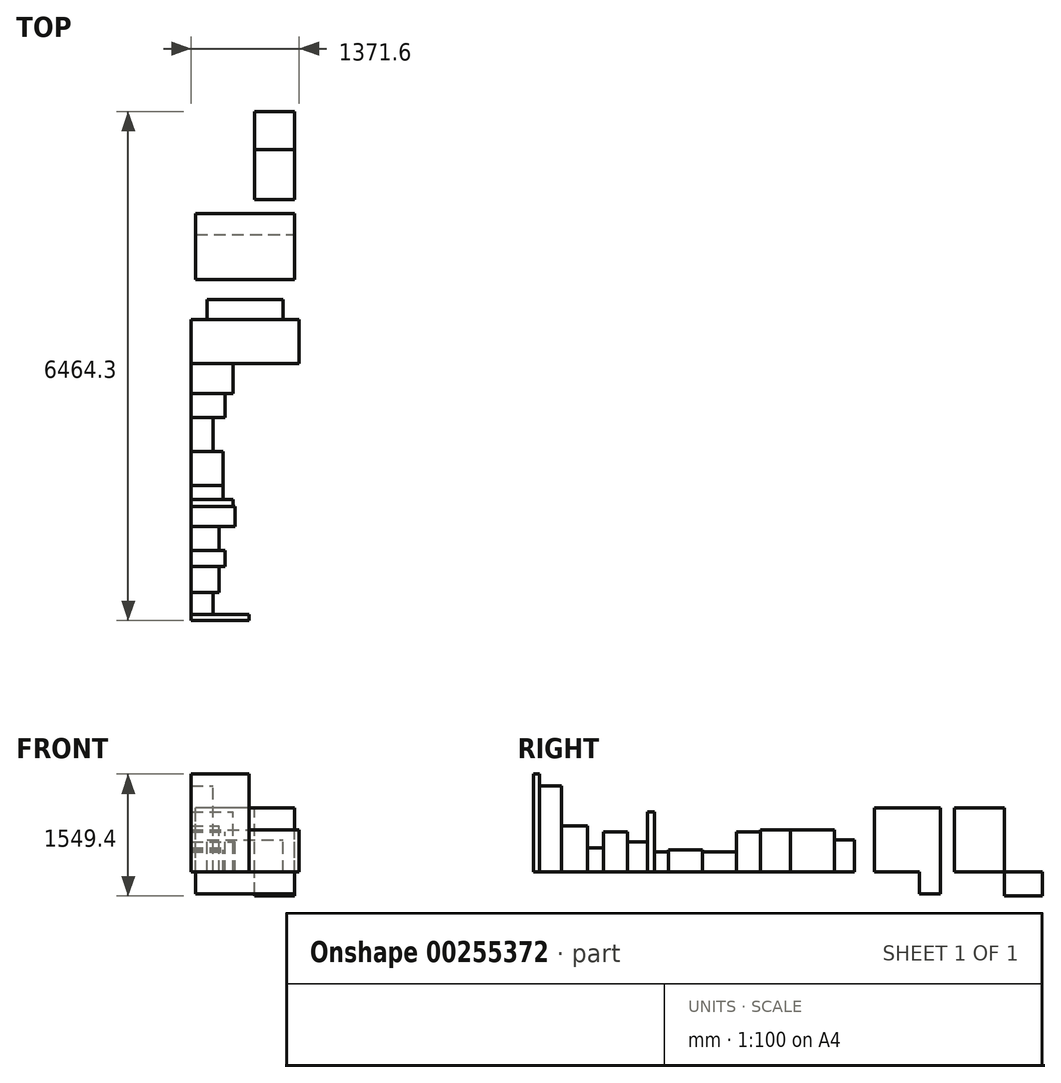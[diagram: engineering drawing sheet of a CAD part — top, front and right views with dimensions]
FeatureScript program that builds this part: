
annotation { "Feature Type Name" : "Feature", "Feature Type Description" : "" }
export const myFeature = defineFeature(function(context is Context, id is Id, definition is map)
    precondition{}
    {
        {
            var Q0;
            Q0=qCreatedBy(makeId("Front.planeOp"),FACE);
            var sketch = newSketch(context, id + "F0", { "sketchPlane" : qUnion([Q0])});
            skLineSegment(sketch, "E0.bottom", {"start": v(0, 0) * mm, "end": v(965.2, 0) * mm});
            skLineSegment(sketch, "E0.top", {"start": v(0, 406.4) * mm, "end": v(965.2, 406.4) * mm});
            skLineSegment(sketch, "E0.left", {"start": v(0, 0) * mm, "end": v(0, 406.4) * mm});
            skLineSegment(sketch, "E0.right", {"start": v(965.2, 0) * mm, "end": v(965.2, 406.4) * mm});
            skSolve(sketch);
        }
        {
            var Q0;
            Q0 = qSketchRegion(id + "F0", true);
            extrude(context, id + "F1", {"entities" : qUnion([Q0]), "depth" : 254 * mm});
        }
        {
            var Q0;
            Q0=makeQuery(id+"F1.opExtrude","CAP_FACE",FACE,{"disambiguationData":[OSD([sQuery(id+"F0.wireOp",EDGE,"E0.bottom"),sQuery(id+"F0.wireOp",EDGE,"E0.top"),sQuery(id+"F0.wireOp",EDGE,"E0.left"),sQuery(id+"F0.wireOp",EDGE,"E0.right")])],"isStart":false});
            var sketch = newSketch(context, id + "F2", { "sketchPlane" : qUnion([Q0])});
            skLineSegment(sketch, "E1.bottom", {"start": v(-203.2, 533.4) * mm, "end": v(1168.4, 533.4) * mm});
            skLineSegment(sketch, "E1.top", {"start": v(-203.2, 0) * mm, "end": v(1168.4, 0) * mm});
            skLineSegment(sketch, "E1.left", {"start": v(-203.2, 533.4) * mm, "end": v(-203.2, 0) * mm});
            skLineSegment(sketch, "E1.right", {"start": v(1168.4, 533.4) * mm, "end": v(1168.4, 0) * mm});
            skSolve(sketch);
        }
        {
            var Q0;
            Q0 = qSketchRegion(id + "F2", true);
            extrude(context, id + "F3", {"entities" : qUnion([Q0]), "operationType" : NewBodyOperationType.ADD, "depth" : 558.8 * mm});
        }
        {
            var Q0;
            Q0=makeQuery(id+"F1.opExtrude","CAP_FACE",FACE,{"disambiguationData":[OSD([sQuery(id+"F0.wireOp",EDGE,"E0.bottom"),sQuery(id+"F0.wireOp",EDGE,"E0.top"),sQuery(id+"F0.wireOp",EDGE,"E0.left"),sQuery(id+"F0.wireOp",EDGE,"E0.right")])],"isStart":true});
            cPlane(context, id + "F4", {"entities" : qUnion([Q0]), "cplaneType" : CPlaneType.OFFSET, "offset" : 254 * mm, "width" : 152.4 * mm, "height" : 152.4 * mm});
        }
        {
            var Q0;
            Q0=qCreatedBy(id+"F4.planeOp",FACE);
            var sketch = newSketch(context, id + "F5", { "sketchPlane" : qUnion([Q0])});
            skLineSegment(sketch, "E2.bottom", {"start": v(-1111.25, 0) * mm, "end": v(146.05, 0) * mm});
            skLineSegment(sketch, "E2.top", {"start": v(-1111.25, 812.8) * mm, "end": v(146.05, 812.8) * mm});
            skLineSegment(sketch, "E2.left", {"start": v(-1111.25, 0) * mm, "end": v(-1111.25, 812.8) * mm});
            skLineSegment(sketch, "E2.right", {"start": v(146.05, 0) * mm, "end": v(146.05, 812.8) * mm});
            skSolve(sketch);
        }
        {
            var Q0;
            Q0 = qSketchRegion(id + "F5", true);
            extrude(context, id + "F6", {"entities" : qUnion([Q0]), "depth" : 838.2 * mm});
        }
        {
            var Q0;
            Q0=makeQuery(id+"F6.opExtrude","SWEPT_FACE",FACE,{"disambiguationData":[OSD([sQuery(id+"F5.wireOp",EDGE,"E2.bottom")])]});
            var sketch = newSketch(context, id + "F7", { "sketchPlane" : qUnion([Q0])});
            skLineSegment(sketch, "E3.bottom", {"start": v(-146.05, -1092.2) * mm, "end": v(1111.25, -1092.2) * mm});
            skLineSegment(sketch, "E3.top", {"start": v(-146.05, -825.5) * mm, "end": v(1111.25, -825.5) * mm});
            skLineSegment(sketch, "E3.left", {"start": v(-146.05, -1092.2) * mm, "end": v(-146.05, -825.5) * mm});
            skLineSegment(sketch, "E3.right", {"start": v(1111.25, -1092.2) * mm, "end": v(1111.25, -825.5) * mm});
            skSolve(sketch);
        }
        {
            var Q0;
            Q0 = qSketchRegion(id + "F7", true);
            extrude(context, id + "F8", {"entities" : qUnion([Q0]), "operationType" : NewBodyOperationType.ADD, "depth" : 279.4 * mm});
        }
        {
            var Q0;
            Q0=makeQuery(id+"F8.boolean.opBoolean","MERGE",FACE,{"derivedFrom":[makeQuery(id+"F6.opExtrude","CAP_FACE",FACE,{"disambiguationData":[OSD([sQuery(id+"F5.wireOp",EDGE,"E2.bottom"),sQuery(id+"F5.wireOp",EDGE,"E2.top"),sQuery(id+"F5.wireOp",EDGE,"E2.left"),sQuery(id+"F5.wireOp",EDGE,"E2.right")])],"isStart":false}),makeQuery(id+"F8.opExtrude","SWEPT_FACE",FACE,{"disambiguationData":[OSD([sQuery(id+"F7.wireOp",EDGE,"E3.bottom")])]})]});
            cPlane(context, id + "F9", {"entities" : qUnion([Q0]), "cplaneType" : CPlaneType.OFFSET, "offset" : 177.8 * mm, "width" : 152.4 * mm, "height" : 152.4 * mm});
        }
        {
            var Q0;
            Q0=qCreatedBy(id+"F9.planeOp",FACE);
            var sketch = newSketch(context, id + "F10", { "sketchPlane" : qUnion([Q0])});
            skLineSegment(sketch, "E4.bottom", {"start": v(-1111.25, 0) * mm, "end": v(-603.25, 0) * mm});
            skLineSegment(sketch, "E4.top", {"start": v(-1111.25, 812.8) * mm, "end": v(-603.25, 812.8) * mm});
            skLineSegment(sketch, "E4.left", {"start": v(-1111.25, 0) * mm, "end": v(-1111.25, 812.8) * mm});
            skLineSegment(sketch, "E4.right", {"start": v(-603.25, 0) * mm, "end": v(-603.25, 812.8) * mm});
            skSolve(sketch);
        }
        {
            var Q0;
            Q0 = qSketchRegion(id + "F10", true);
            extrude(context, id + "F11", {"entities" : qUnion([Q0]), "depth" : 635 * mm});
        }
        {
            var Q0;
            Q0=makeQuery(id+"F11.opExtrude","SWEPT_FACE",FACE,{"disambiguationData":[OSD([sQuery(id+"F10.wireOp",EDGE,"E4.bottom")])]});
            var sketch = newSketch(context, id + "F12", { "sketchPlane" : qUnion([Q0])});
            skLineSegment(sketch, "E5.bottom", {"start": v(603.25, -1905) * mm, "end": v(1111.25, -1905) * mm});
            skLineSegment(sketch, "E5.top", {"start": v(603.25, -2387.6) * mm, "end": v(1111.25, -2387.6) * mm});
            skLineSegment(sketch, "E5.left", {"start": v(603.25, -1905) * mm, "end": v(603.25, -2387.6) * mm});
            skLineSegment(sketch, "E5.right", {"start": v(1111.25, -1905) * mm, "end": v(1111.25, -2387.6) * mm});
            skSolve(sketch);
        }
        {
            var Q0;
            Q0 = qSketchRegion(id + "F12", true);
            extrude(context, id + "F13", {"entities" : qUnion([Q0]), "depth" : 304.8 * mm});
        }
        {
            var Q0;
            Q0=makeQuery(id+"F3.opExtrude","CAP_FACE",FACE,{"disambiguationData":[OSD([sQuery(id+"F2.wireOp",EDGE,"E1.bottom"),sQuery(id+"F2.wireOp",EDGE,"E1.top"),sQuery(id+"F2.wireOp",EDGE,"E1.left"),sQuery(id+"F2.wireOp",EDGE,"E1.right")])],"isStart":false});
            var sketch = newSketch(context, id + "F14", { "sketchPlane" : qUnion([Q0])});
            skLineSegment(sketch, "E6.bottom", {"start": v(-203.2, 0) * mm, "end": v(330.2, 0) * mm});
            skLineSegment(sketch, "E6.top", {"start": v(-203.2, 533.4) * mm, "end": v(330.2, 533.4) * mm});
            skLineSegment(sketch, "E6.left", {"start": v(-203.2, 0) * mm, "end": v(-203.2, 533.4) * mm});
            skLineSegment(sketch, "E6.right", {"start": v(330.2, 0) * mm, "end": v(330.2, 533.4) * mm});
            skSolve(sketch);
        }
        {
            var Q0;
            Q0 = qSketchRegion(id + "F14", true);
            extrude(context, id + "F15", {"entities" : qUnion([Q0]), "depth" : 381 * mm});
        }
        {
            var Q0;
            Q0=makeQuery(id+"F15.opExtrude","CAP_FACE",FACE,{"disambiguationData":[OSD([sQuery(id+"F14.wireOp",EDGE,"E6.bottom"),sQuery(id+"F14.wireOp",EDGE,"E6.top"),sQuery(id+"F14.wireOp",EDGE,"E6.left"),sQuery(id+"F14.wireOp",EDGE,"E6.right")])],"isStart":false});
            var sketch = newSketch(context, id + "F16", { "sketchPlane" : qUnion([Q0])});
            skLineSegment(sketch, "E7.bottom", {"start": v(-203.2, 0) * mm, "end": v(228.6, 0) * mm});
            skLineSegment(sketch, "E7.top", {"start": v(-203.2, 508) * mm, "end": v(228.6, 508) * mm});
            skLineSegment(sketch, "E7.left", {"start": v(-203.2, 0) * mm, "end": v(-203.2, 508) * mm});
            skLineSegment(sketch, "E7.right", {"start": v(228.6, 0) * mm, "end": v(228.6, 508) * mm});
            skSolve(sketch);
        }
        {
            var Q0;
            Q0 = qSketchRegion(id + "F16", true);
            extrude(context, id + "F17", {"entities" : qUnion([Q0]), "depth" : 304.8 * mm});
        }
        {
            var Q0;
            Q0=makeQuery(id+"F17.opExtrude","CAP_FACE",FACE,{"disambiguationData":[OSD([sQuery(id+"F16.wireOp",EDGE,"E7.bottom"),sQuery(id+"F16.wireOp",EDGE,"E7.top"),sQuery(id+"F16.wireOp",EDGE,"E7.left"),sQuery(id+"F16.wireOp",EDGE,"E7.right")])],"isStart":false});
            var sketch = newSketch(context, id + "F18", { "sketchPlane" : qUnion([Q0])});
            skLineSegment(sketch, "E8.bottom", {"start": v(-203.2, 0) * mm, "end": v(76.2, 0) * mm});
            skLineSegment(sketch, "E8.top", {"start": v(-203.2, 254) * mm, "end": v(76.2, 254) * mm});
            skLineSegment(sketch, "E8.left", {"start": v(-203.2, 0) * mm, "end": v(-203.2, 254) * mm});
            skLineSegment(sketch, "E8.right", {"start": v(76.2, 0) * mm, "end": v(76.2, 254) * mm});
            skSolve(sketch);
        }
        {
            var Q0;
            Q0 = qSketchRegion(id + "F18", true);
            extrude(context, id + "F19", {"entities" : qUnion([Q0]), "depth" : 431.8 * mm});
        }
        {
            var Q0;
            Q0=makeQuery(id+"F19.opExtrude","CAP_FACE",FACE,{"disambiguationData":[OSD([sQuery(id+"F18.wireOp",EDGE,"E8.bottom"),sQuery(id+"F18.wireOp",EDGE,"E8.top"),sQuery(id+"F18.wireOp",EDGE,"E8.left"),sQuery(id+"F18.wireOp",EDGE,"E8.right")])],"isStart":false});
            var sketch = newSketch(context, id + "F20", { "sketchPlane" : qUnion([Q0])});
            skLineSegment(sketch, "E9.bottom", {"start": v(-203.2, 0) * mm, "end": v(203.2, 0) * mm});
            skLineSegment(sketch, "E9.top", {"start": v(-203.2, 279.4) * mm, "end": v(203.2, 279.4) * mm});
            skLineSegment(sketch, "E9.left", {"start": v(-203.2, 0) * mm, "end": v(-203.2, 279.4) * mm});
            skLineSegment(sketch, "E9.right", {"start": v(203.2, 0) * mm, "end": v(203.2, 279.4) * mm});
            skSolve(sketch);
        }
        {
            var Q0;
            Q0 = qSketchRegion(id + "F20", true);
            extrude(context, id + "F21", {"entities" : qUnion([Q0]), "depth" : 431.8 * mm});
        }
        {
            var Q0;
            Q0=makeQuery(id+"F21.opExtrude","CAP_FACE",FACE,{"disambiguationData":[OSD([sQuery(id+"F20.wireOp",EDGE,"E9.bottom"),sQuery(id+"F20.wireOp",EDGE,"E9.top"),sQuery(id+"F20.wireOp",EDGE,"E9.left"),sQuery(id+"F20.wireOp",EDGE,"E9.right")])],"isStart":false});
            var sketch = newSketch(context, id + "F22", { "sketchPlane" : qUnion([Q0])});
            skLineSegment(sketch, "E10.bottom", {"start": v(-203.2, 0) * mm, "end": v(203.2, 0) * mm});
            skLineSegment(sketch, "E10.top", {"start": v(-203.2, 254) * mm, "end": v(203.2, 254) * mm});
            skLineSegment(sketch, "E10.left", {"start": v(-203.2, 0) * mm, "end": v(-203.2, 254) * mm});
            skLineSegment(sketch, "E10.right", {"start": v(203.2, 0) * mm, "end": v(203.2, 254) * mm});
            skSolve(sketch);
        }
        {
            var Q0;
            Q0 = qSketchRegion(id + "F22", true);
            extrude(context, id + "F23", {"entities" : qUnion([Q0]), "depth" : 177.8 * mm});
        }
        {
            var Q0;
            Q0=makeQuery(id+"F23.opExtrude","CAP_FACE",FACE,{"disambiguationData":[OSD([sQuery(id+"F22.wireOp",EDGE,"E10.bottom"),sQuery(id+"F22.wireOp",EDGE,"E10.top"),sQuery(id+"F22.wireOp",EDGE,"E10.left"),sQuery(id+"F22.wireOp",EDGE,"E10.right")])],"isStart":false});
            var sketch = newSketch(context, id + "F24", { "sketchPlane" : qUnion([Q0])});
            skLineSegment(sketch, "E11.bottom", {"start": v(-203.2, 0) * mm, "end": v(330.2, 0) * mm});
            skLineSegment(sketch, "E11.top", {"start": v(-203.2, 762) * mm, "end": v(330.2, 762) * mm});
            skLineSegment(sketch, "E11.left", {"start": v(-203.2, 0) * mm, "end": v(-203.2, 762) * mm});
            skLineSegment(sketch, "E11.right", {"start": v(330.2, 0) * mm, "end": v(330.2, 762) * mm});
            skSolve(sketch);
        }
        {
            var Q0;
            Q0 = qSketchRegion(id + "F24", true);
            extrude(context, id + "F25", {"entities" : qUnion([Q0]), "depth" : 88.9 * mm});
        }
        {
            var Q0;
            Q0=makeQuery(id+"F25.opExtrude","CAP_FACE",FACE,{"disambiguationData":[OSD([sQuery(id+"F24.wireOp",EDGE,"E11.bottom"),sQuery(id+"F24.wireOp",EDGE,"E11.top"),sQuery(id+"F24.wireOp",EDGE,"E11.left"),sQuery(id+"F24.wireOp",EDGE,"E11.right")])],"isStart":false});
            var sketch = newSketch(context, id + "F26", { "sketchPlane" : qUnion([Q0])});
            skLineSegment(sketch, "E12.bottom", {"start": v(-203.2, 0) * mm, "end": v(355.6, 0) * mm});
            skLineSegment(sketch, "E12.top", {"start": v(-203.2, 381) * mm, "end": v(355.6, 381) * mm});
            skLineSegment(sketch, "E12.left", {"start": v(-203.2, 0) * mm, "end": v(-203.2, 381) * mm});
            skLineSegment(sketch, "E12.right", {"start": v(355.6, 0) * mm, "end": v(355.6, 381) * mm});
            skSolve(sketch);
        }
        {
            var Q0;
            Q0 = qSketchRegion(id + "F26", true);
            extrude(context, id + "F27", {"entities" : qUnion([Q0]), "depth" : 254 * mm});
        }
        {
            var Q0;
            Q0=makeQuery(id+"F27.opExtrude","CAP_FACE",FACE,{"disambiguationData":[OSD([sQuery(id+"F26.wireOp",EDGE,"E12.bottom"),sQuery(id+"F26.wireOp",EDGE,"E12.top"),sQuery(id+"F26.wireOp",EDGE,"E12.left"),sQuery(id+"F26.wireOp",EDGE,"E12.right")])],"isStart":false});
            var sketch = newSketch(context, id + "F28", { "sketchPlane" : qUnion([Q0])});
            skLineSegment(sketch, "E13.bottom", {"start": v(-203.2, 0) * mm, "end": v(152.4, 0) * mm});
            skLineSegment(sketch, "E13.top", {"start": v(-203.2, 508) * mm, "end": v(152.4, 508) * mm});
            skLineSegment(sketch, "E13.left", {"start": v(-203.2, 0) * mm, "end": v(-203.2, 508) * mm});
            skLineSegment(sketch, "E13.right", {"start": v(152.4, 0) * mm, "end": v(152.4, 508) * mm});
            skSolve(sketch);
        }
        {
            var Q0;
            Q0 = qSketchRegion(id + "F28", true);
            extrude(context, id + "F29", {"entities" : qUnion([Q0]), "depth" : 304.8 * mm});
        }
        {
            var Q0;
            Q0=makeQuery(id+"F29.opExtrude","CAP_FACE",FACE,{"disambiguationData":[OSD([sQuery(id+"F28.wireOp",EDGE,"E13.bottom"),sQuery(id+"F28.wireOp",EDGE,"E13.top"),sQuery(id+"F28.wireOp",EDGE,"E13.left"),sQuery(id+"F28.wireOp",EDGE,"E13.right")])],"isStart":false});
            var sketch = newSketch(context, id + "F30", { "sketchPlane" : qUnion([Q0])});
            skLineSegment(sketch, "E14.bottom", {"start": v(-203.2, 0) * mm, "end": v(228.6, 0) * mm});
            skLineSegment(sketch, "E14.top", {"start": v(-203.2, 304.8) * mm, "end": v(228.6, 304.8) * mm});
            skLineSegment(sketch, "E14.left", {"start": v(-203.2, 0) * mm, "end": v(-203.2, 304.8) * mm});
            skLineSegment(sketch, "E14.right", {"start": v(228.6, 0) * mm, "end": v(228.6, 304.8) * mm});
            skSolve(sketch);
        }
        {
            var Q0;
            Q0 = qSketchRegion(id + "F30", true);
            extrude(context, id + "F31", {"entities" : qUnion([Q0]), "depth" : 203.2 * mm});
        }
        {
            var Q0;
            Q0=makeQuery(id+"F31.opExtrude","CAP_FACE",FACE,{"disambiguationData":[OSD([sQuery(id+"F30.wireOp",EDGE,"E14.bottom"),sQuery(id+"F30.wireOp",EDGE,"E14.top"),sQuery(id+"F30.wireOp",EDGE,"E14.left"),sQuery(id+"F30.wireOp",EDGE,"E14.right")])],"isStart":false});
            var sketch = newSketch(context, id + "F32", { "sketchPlane" : qUnion([Q0])});
            skLineSegment(sketch, "E15.bottom", {"start": v(-203.2, 0) * mm, "end": v(152.4, 0) * mm});
            skLineSegment(sketch, "E15.top", {"start": v(-203.2, 584.2) * mm, "end": v(152.4, 584.2) * mm});
            skLineSegment(sketch, "E15.left", {"start": v(-203.2, 0) * mm, "end": v(-203.2, 584.2) * mm});
            skLineSegment(sketch, "E15.right", {"start": v(152.4, 0) * mm, "end": v(152.4, 584.2) * mm});
            skSolve(sketch);
        }
        {
            var Q0;
            Q0 = qSketchRegion(id + "F32", true);
            extrude(context, id + "F33", {"entities" : qUnion([Q0]), "depth" : 330.2 * mm});
        }
        {
            var Q0;
            Q0=makeQuery(id+"F33.opExtrude","CAP_FACE",FACE,{"disambiguationData":[OSD([sQuery(id+"F32.wireOp",EDGE,"E15.bottom"),sQuery(id+"F32.wireOp",EDGE,"E15.top"),sQuery(id+"F32.wireOp",EDGE,"E15.left"),sQuery(id+"F32.wireOp",EDGE,"E15.right")])],"isStart":false});
            var sketch = newSketch(context, id + "F34", { "sketchPlane" : qUnion([Q0])});
            skLineSegment(sketch, "E16.bottom", {"start": v(-203.2, 0) * mm, "end": v(76.2, 0) * mm});
            skLineSegment(sketch, "E16.top", {"start": v(-203.2, 1092.2) * mm, "end": v(76.2, 1092.2) * mm});
            skLineSegment(sketch, "E16.left", {"start": v(-203.2, 0) * mm, "end": v(-203.2, 1092.2) * mm});
            skLineSegment(sketch, "E16.right", {"start": v(76.2, 0) * mm, "end": v(76.2, 1092.2) * mm});
            skSolve(sketch);
        }
        {
            var Q0;
            Q0 = qSketchRegion(id + "F34", true);
            extrude(context, id + "F35", {"entities" : qUnion([Q0]), "depth" : 279.4 * mm});
        }
        {
            var Q0;
            Q0=makeQuery(id+"F35.opExtrude","CAP_FACE",FACE,{"disambiguationData":[OSD([sQuery(id+"F34.wireOp",EDGE,"E16.bottom"),sQuery(id+"F34.wireOp",EDGE,"E16.top"),sQuery(id+"F34.wireOp",EDGE,"E16.left"),sQuery(id+"F34.wireOp",EDGE,"E16.right")])],"isStart":false});
            var sketch = newSketch(context, id + "F36", { "sketchPlane" : qUnion([Q0])});
            skLineSegment(sketch, "E17.bottom", {"start": v(-203.2, 0) * mm, "end": v(533.4, 0) * mm});
            skLineSegment(sketch, "E17.top", {"start": v(-203.2, 1244.6) * mm, "end": v(533.4, 1244.6) * mm});
            skLineSegment(sketch, "E17.left", {"start": v(-203.2, 0) * mm, "end": v(-203.2, 1244.6) * mm});
            skLineSegment(sketch, "E17.right", {"start": v(533.4, 0) * mm, "end": v(533.4, 1244.6) * mm});
            skSolve(sketch);
        }
        {
            var Q0;
            Q0 = qSketchRegion(id + "F36", true);
            extrude(context, id + "F37", {"entities" : qUnion([Q0]), "depth" : 76.2 * mm});
        }
    });
